# Revit family: Toilet_Seat-Elongated_Closed_Front-KOHLER-Brevia-K-20110_1
name_source: partatom
category: Specialty Equipment
revit_build: Autodesk Revit 2015 (Build: 20140606_1530(x64)
units: mm (PartAtom-declared; Revit-internal decimal feet)

## types (2) — shared parameters
ADA Compliant = No
Assembly Code = C1030200
Date Modified = 02/05/2019
Default Elevation = 0"
Description = Quite-Close Elongated Toilet Seat
Height = 13/16"
Length = 18"
Manufacturer = KOHLER Co.
MasterFormat 1995 = 10820
MasterFormat 2004 = 10.28.13
Material = Plastic
Product Documentation Link = https://www.us.kohler.com
Product Name = Brevia
Product Page URL = http://www.us.kohler.com
URL = https://www.us.kohler.com
WaterSense Certified = No
Width = 14 3/16"

## per-type parameters (varying)
| type | Finish | Model | Type |
| 0-White | Kohler-Plastic-0-White | K-20110-0 | 1 |
| 96-Biscuit | Kohler-Plastic-96-Biscuit | K-20110-96 | 2 |

## geometry (parser evidence)
native form markers: Sweep x4
no freeform markers — native parametric forms only
